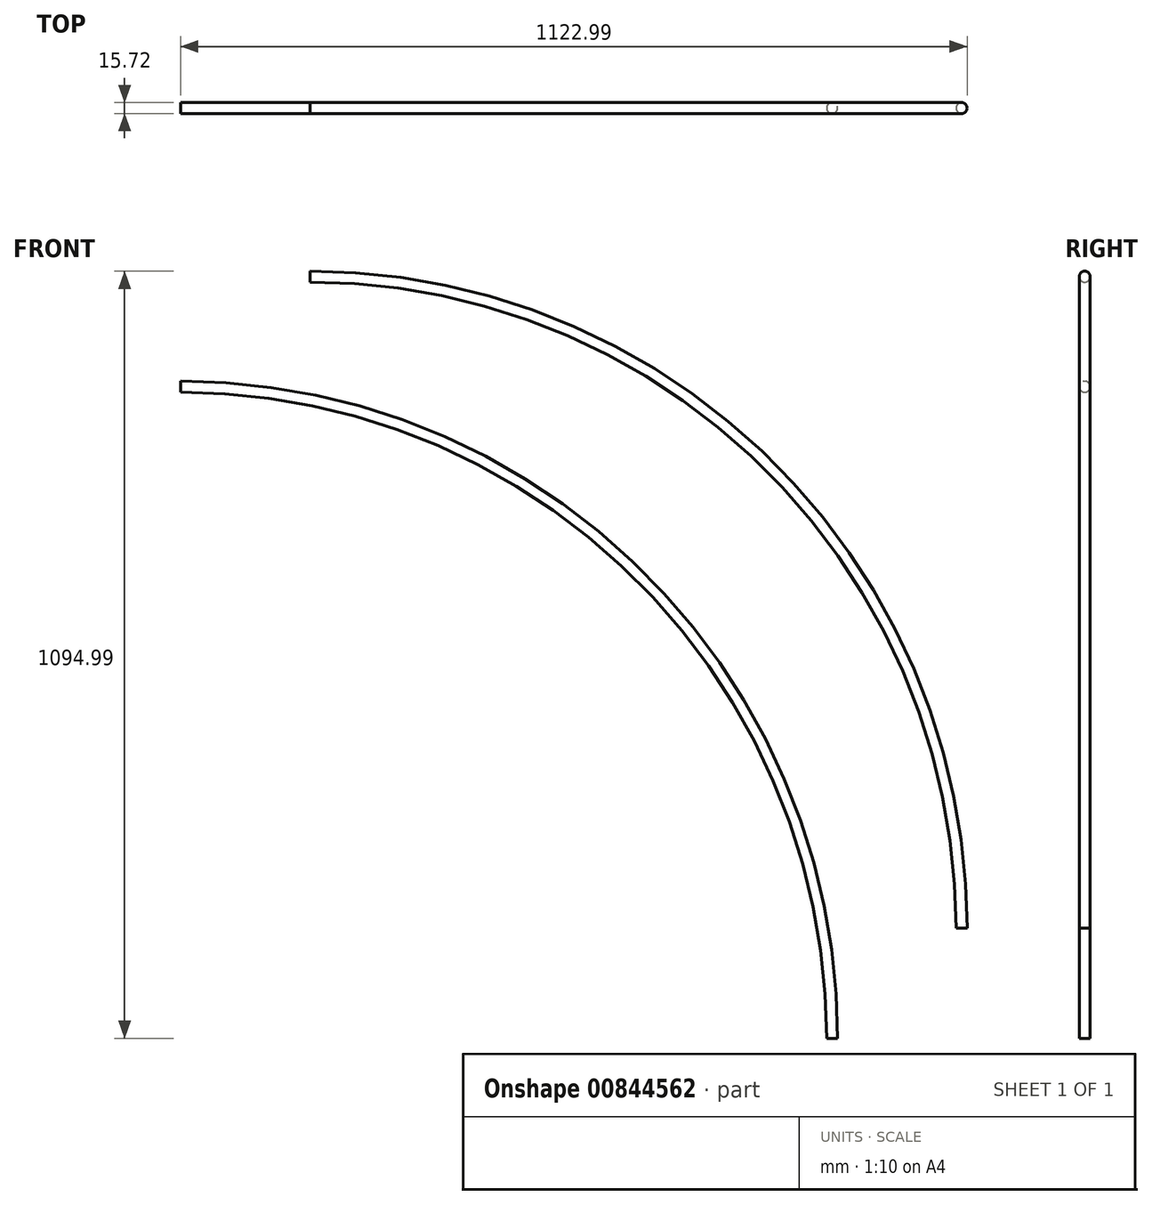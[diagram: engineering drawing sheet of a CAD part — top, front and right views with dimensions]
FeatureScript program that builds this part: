
annotation { "Feature Type Name" : "Feature", "Feature Type Description" : "" }
export const myFeature = defineFeature(function(context is Context, id is Id, definition is map)
    precondition{}
    {
        {
            var Q0;
            Q0=qCreatedBy(makeId("Front.planeOp"),FACE);
            var sketch = newSketch(context, id + "F0", { "sketchPlane" : qUnion([Q0])});
            skArc(sketch, "E0", {"start": v(0, 930) * mm, "mid": v(657.6, 657.6) * mm, "end": v(930, 0) * mm});
            skSolve(sketch);
        }
        {
            var Q0;
            Q0=qCreatedBy(makeId("Right.planeOp"),FACE);
            var sketch = newSketch(context, id + "F1", { "sketchPlane" : qUnion([Q0])});
            skCircle(sketch, "E1", {"center": v(0, 182.95) * mm, "radius": 8 * mm});
            skCircle(sketch, "E2", {"center": v(0, 930.13) * mm, "radius": 7.86 * mm});
            skSolve(sketch);
        }
        {
            var Q0;
            Q0=makeQuery(id+"F1.imprint","IMPRINT",FACE,{"disambiguationData":[TD([[makeQuery(id+"F1.imprint","IMPRINT",EDGE,{"derivedFrom":sQuery(id+"F1.wireOp",EDGE,"E2")}),1.0]])]});
            var Q1;
            Q1=sQuery(id+"F0.wireOp",EDGE,"E0");
            sweep(context, id + "F2", {"profiles" : qUnion([Q0]), "path" : qUnion([Q1])});
        }
        {
            var Q0;
            Q0=makeQuery(id+"F2.opSweep","SWEPT_BODY",BODY,{"disambiguationData":[OSD([sQuery(id+"F0.wireOp",EDGE,"E0"),sQuery(id+"F1.wireOp",EDGE,"E2")])]});
            transform(context, id + "F3", {"entities" : qUnion([Q0]), "transformType" : TransformType.TRANSLATION_3D, "dx" : 185 * mm, "dy" : 0 * mm, "dz" : 157 * mm, "makeCopy" : true});
        }
    });
